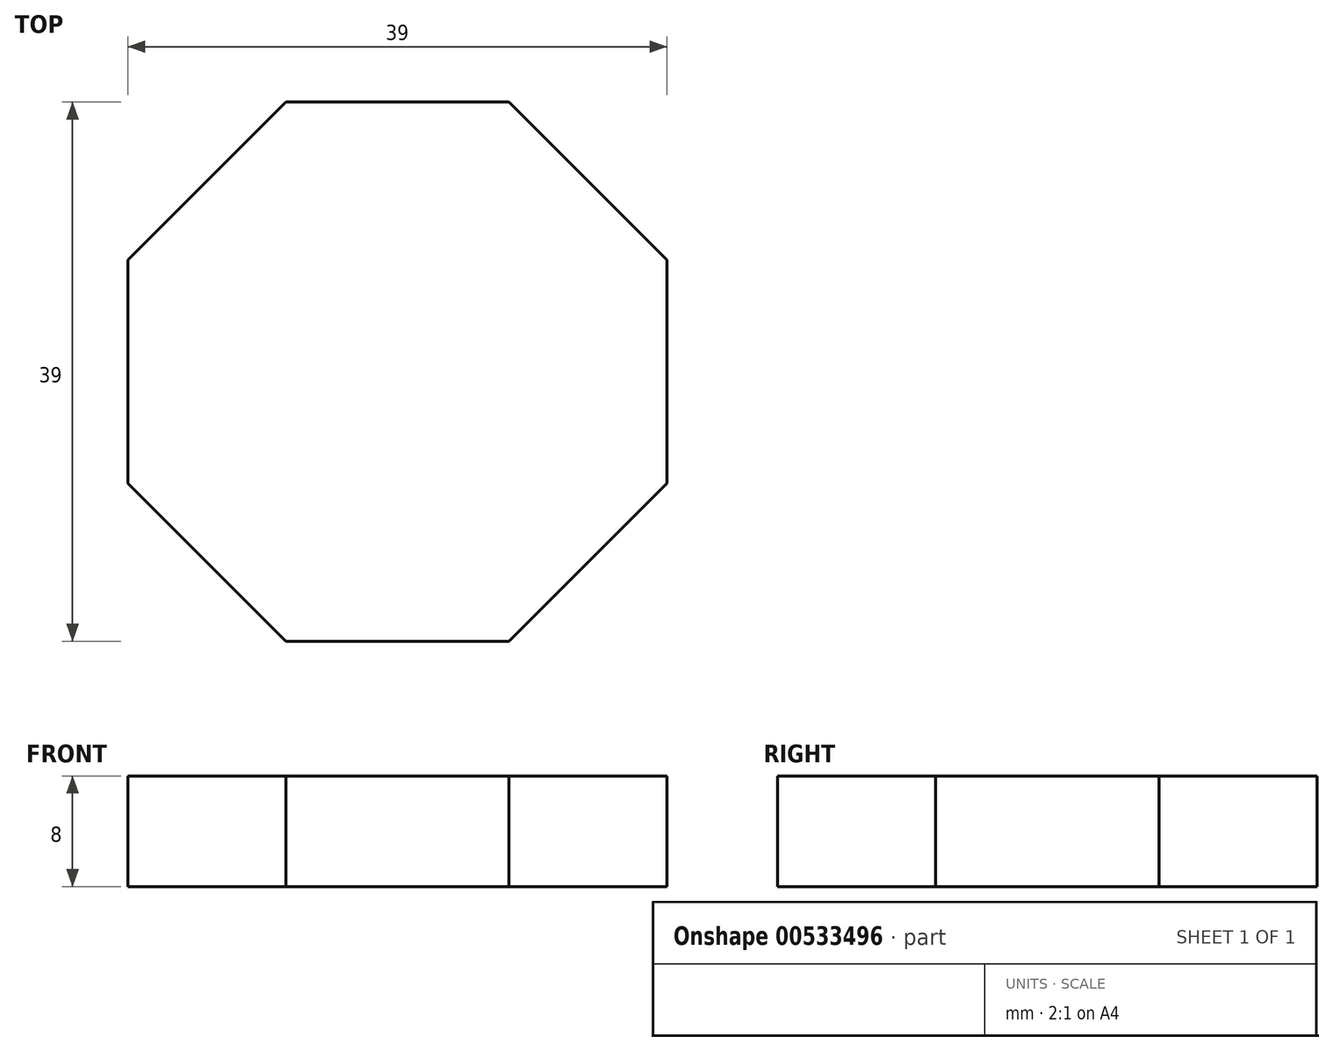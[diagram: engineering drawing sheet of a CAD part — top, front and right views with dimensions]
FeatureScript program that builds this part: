
annotation { "Feature Type Name" : "Feature", "Feature Type Description" : "" }
export const myFeature = defineFeature(function(context is Context, id is Id, definition is map)
    precondition{}
    {
        {
            var Q0;
            Q0=qCreatedBy(makeId("Top.planeOp"),FACE);
            var sketch = newSketch(context, id + "F0", { "sketchPlane" : qUnion([Q0])});
            skCircle(sketch, "E0.cCircle", {"center": v(0, 0) * mm, "radius": 19.5 * mm, "construction": true});
            skLineSegment(sketch, "E0.0", {"start": v(-8.08, 19.5) * mm, "end": v(8.08, 19.5) * mm});
            skLineSegment(sketch, "E0.1", {"start": v(8.08, 19.5) * mm, "end": v(19.5, 8.08) * mm});
            skLineSegment(sketch, "E0.2", {"start": v(19.5, 8.08) * mm, "end": v(19.5, -8.08) * mm});
            skLineSegment(sketch, "E0.3", {"start": v(19.5, -8.08) * mm, "end": v(8.08, -19.5) * mm});
            skLineSegment(sketch, "E0.4", {"start": v(8.08, -19.5) * mm, "end": v(-8.08, -19.5) * mm});
            skLineSegment(sketch, "E0.5", {"start": v(-8.08, -19.5) * mm, "end": v(-19.5, -8.08) * mm});
            skLineSegment(sketch, "E0.6", {"start": v(-19.5, -8.08) * mm, "end": v(-19.5, 8.08) * mm});
            skLineSegment(sketch, "E0.7", {"start": v(-19.5, 8.08) * mm, "end": v(-8.08, 19.5) * mm});
            skPoint(sketch, "E0.0.midPoint", {"position": v(0, 19.5) * mm});
            skSolve(sketch);
        }
        {
            var Q0;
            Q0=qSketchRegion(id+"F0",true);
            extrude(context, id + "F1", {"entities" : qUnion([Q0]), "depth" : 8 * mm, "offsetDistance" : 25 * mm});
        }
    });
